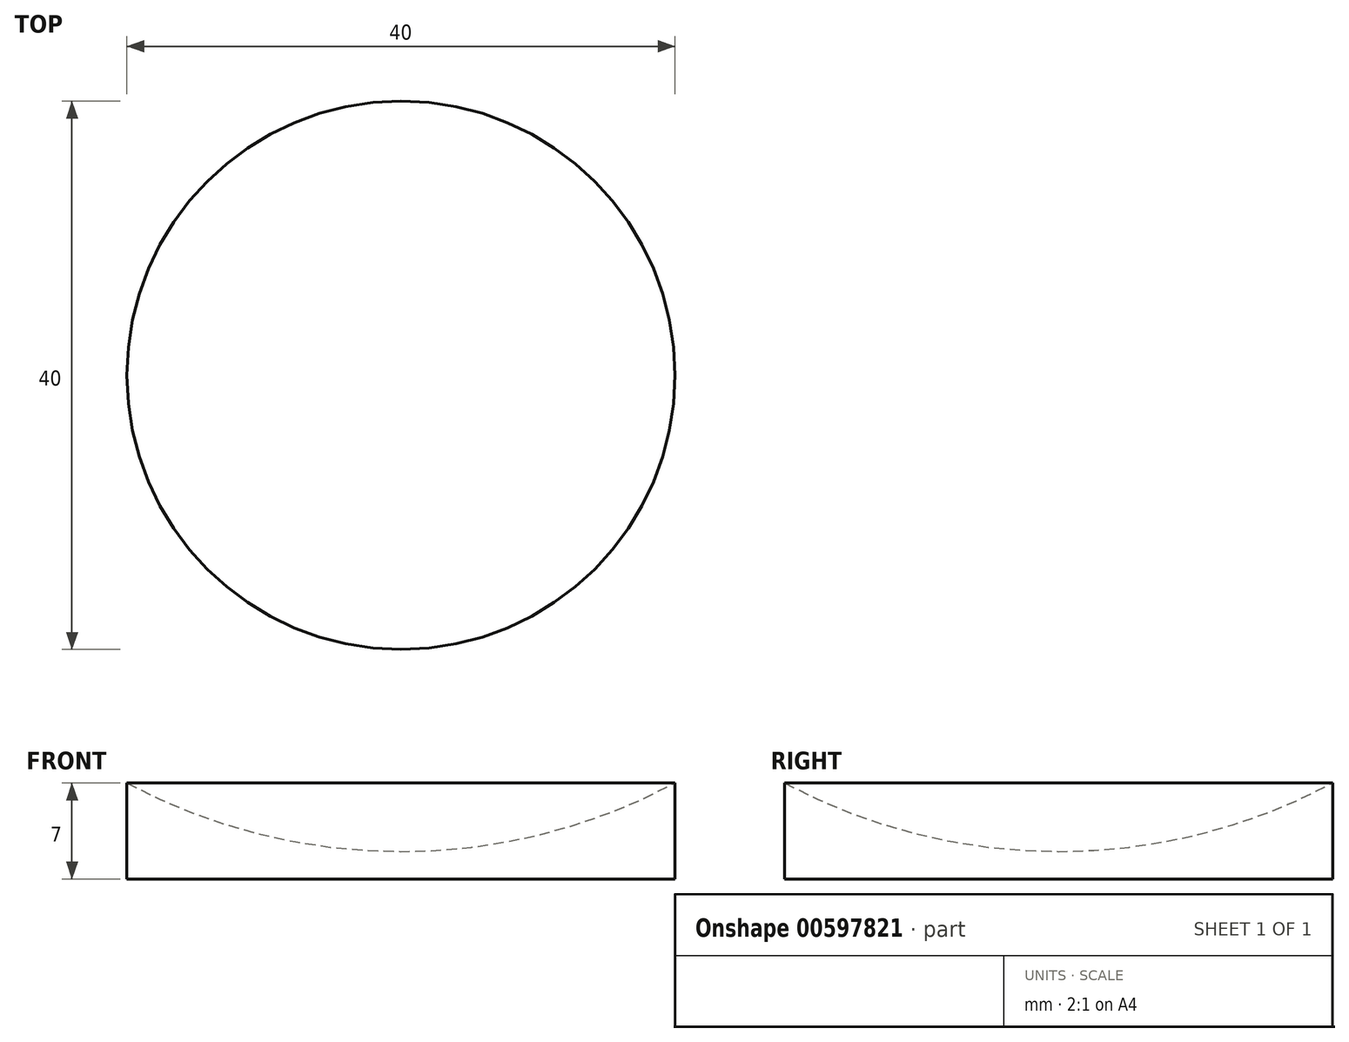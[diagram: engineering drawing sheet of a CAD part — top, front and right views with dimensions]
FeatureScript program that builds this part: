
annotation { "Feature Type Name" : "Feature", "Feature Type Description" : "" }
export const myFeature = defineFeature(function(context is Context, id is Id, definition is map)
    precondition{}
    {
        {
            var Q0;
            Q0=qCreatedBy(makeId("Front.planeOp"),FACE);
            var sketch = newSketch(context, id + "F0", { "sketchPlane" : qUnion([Q0])});
            skCircle(sketch, "E0", {"center": v(0, 0) * mm, "radius": 42.5 * mm});
            skLineSegment(sketch, "E1", {"start": v(-20, -37.5) * mm, "end": v(20, -37.5) * mm});
            skPoint(sketch, "E2", {"position": v(0, -37.5) * mm});
            skPoint(sketch, "E3", {"position": v(0, -42.5) * mm});
            skLineSegment(sketch, "E4.top", {"start": v(-20, -44.5) * mm, "end": v(20, -44.5) * mm});
            skLineSegment(sketch, "E4.left", {"start": v(-20, -37.5) * mm, "end": v(-20, -44.5) * mm});
            skLineSegment(sketch, "E4.right", {"start": v(20, -37.5) * mm, "end": v(20, -44.5) * mm});
            skSolve(sketch);
        }
        {
            var Q0;
            Q0=makeQuery(id+"F0.imprint","IMPRINT",FACE,{"disambiguationData":[TD([[makeQuery(id+"F0.imprint","IMPRINT",EDGE,{"derivedFrom":sQuery(id+"F0.wireOp",EDGE,"E4.top")}),1.0]])]});
            var Q1;
            {var subQ0=sQuery(id+"F0.wireOp",EDGE,"E1");Q1=makeQuery(id+"F0.imprint","IMPRINT",FACE,{"disambiguationData":[TD([[makeQuery(id+"F0.imprint","IMPRINT",EDGE,{"derivedFrom":subQ0}),-1.0]])]});}
            extrude(context, id + "F1", {"entities" : qUnion([Q0, Q1]), "depth" : 20 * mm, "offsetDistance" : 25 * mm, "hasSecondDirection" : true, "secondDirectionOppositeDirection" : true, "secondDirectionDepth" : 20 * mm});
        }
        {
            var Q0;
            Q0=qCreatedBy(makeId("Front.planeOp"),FACE);
            var sketch = newSketch(context, id + "F2", { "sketchPlane" : qUnion([Q0])});
            skCircle(sketch, "E5", {"center": v(0, 0) * mm, "radius": 42.5 * mm});
            skLineSegment(sketch, "E6", {"start": v(-20, -37.5) * mm, "end": v(20, -37.5) * mm});
            skPoint(sketch, "E7", {"position": v(0, -37.5) * mm});
            skPoint(sketch, "E8", {"position": v(0, -42.5) * mm});
            skLineSegment(sketch, "E9.top", {"start": v(-20, -44.5) * mm, "end": v(20, -44.5) * mm});
            skLineSegment(sketch, "E9.left", {"start": v(-20, -37.5) * mm, "end": v(-20, -44.5) * mm});
            skLineSegment(sketch, "E9.right", {"start": v(20, -37.5) * mm, "end": v(20, -44.5) * mm});
            skSolve(sketch);
        }
        {
            var Q0;
            Q0=qCreatedBy(makeId("Top.planeOp"),FACE);
            var sketch = newSketch(context, id + "F3", { "sketchPlane" : qUnion([Q0])});
            skCircle(sketch, "E10", {"center": v(0, 0) * mm, "radius": 42.5 * mm});
            skSolve(sketch);
        }
        {
            var Q0;
            Q0 = qSketchRegion(id + "F3", true);
            var Q1;
            Q1=sQuery(id+"F2.wireOp",EDGE,"E5");
            sweep(context, id + "F4", {"operationType" : NewBodyOperationType.REMOVE, "profiles" : qUnion([Q0]), "path" : qUnion([Q1])});
        }
        {
            var Q0;
            Q0=makeQuery(id+"F1.opExtrude","CAP_EDGE",EDGE,{"disambiguationData":[OSD([sQuery(id+"F0.wireOp",EDGE,"E4.left")])],"isStart":false});
            var Q1;
            Q1=makeQuery(id+"F1.opExtrude","CAP_EDGE",EDGE,{"disambiguationData":[OSD([sQuery(id+"F0.wireOp",EDGE,"E4.right")])],"isStart":false});
            var Q2;
            Q2=makeQuery(id+"F1.opExtrude","CAP_EDGE",EDGE,{"disambiguationData":[OSD([sQuery(id+"F0.wireOp",EDGE,"E4.right")])],"isStart":true});
            var Q3;
            Q3=makeQuery(id+"F1.opExtrude","CAP_EDGE",EDGE,{"disambiguationData":[OSD([sQuery(id+"F0.wireOp",EDGE,"E4.left")])],"isStart":true});
            fillet(context, id + "F5", {"entities" : qUnion([Q0, Q1, Q2, Q3]), "radius" : 20 * mm, "tangentPropagation" : true, "allowEdgeOverflow" : false});
        }
    });
